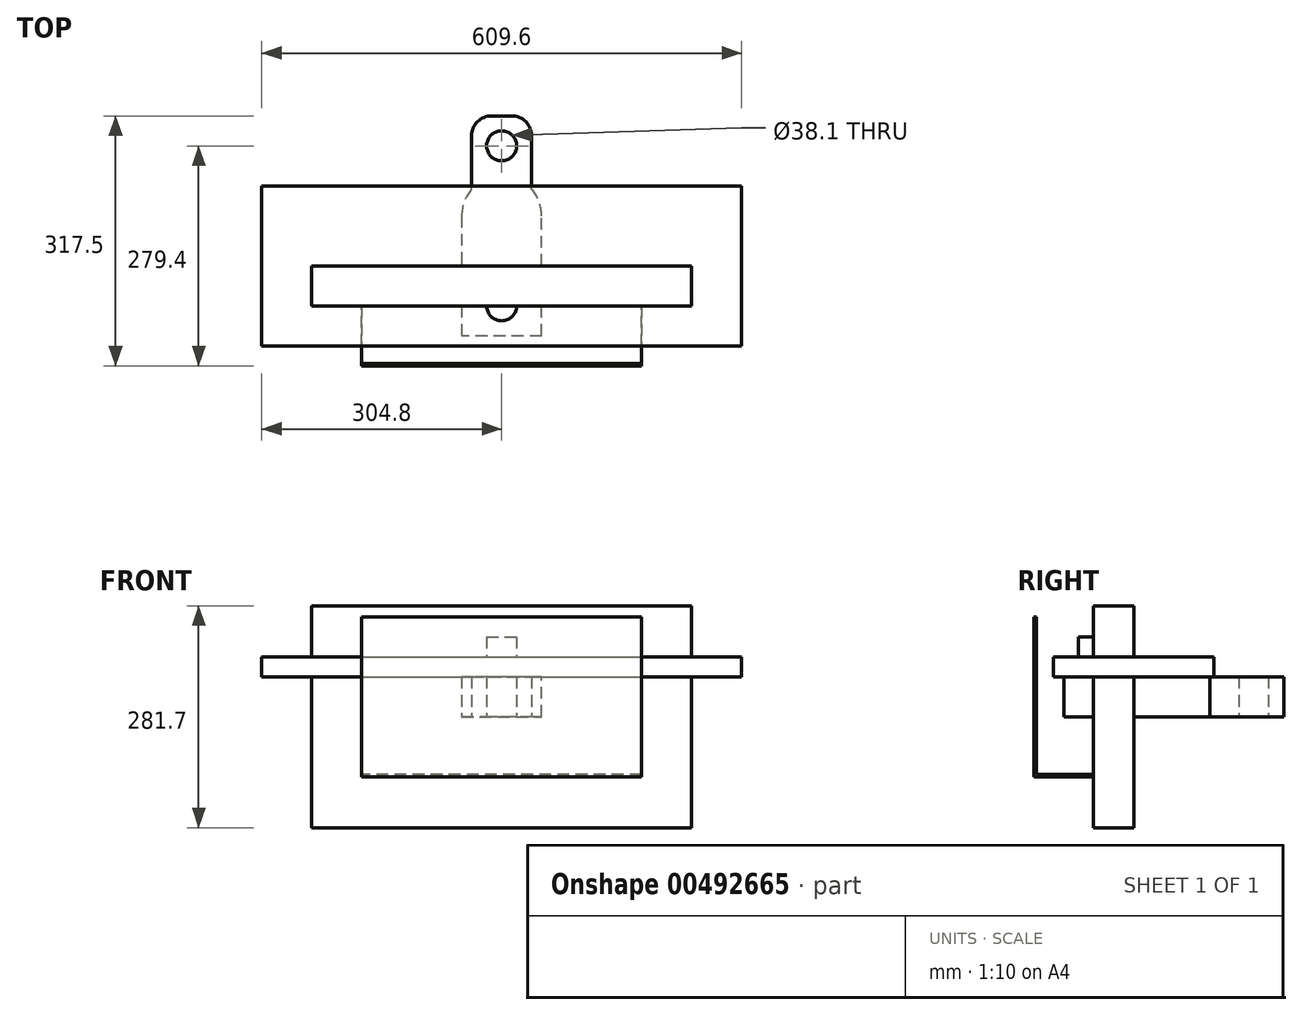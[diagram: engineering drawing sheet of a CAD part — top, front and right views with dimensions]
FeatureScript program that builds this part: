
annotation { "Feature Type Name" : "Feature", "Feature Type Description" : "" }
export const myFeature = defineFeature(function(context is Context, id is Id, definition is map)
    precondition{}
    {
        {
            var Q0;
            Q0=qCreatedBy(makeId("Top.planeOp"),FACE);
            var sketch = newSketch(context, id + "F0", { "sketchPlane" : qUnion([Q0])});
            skCircle(sketch, "E0", {"center": v(0, 0) * mm, "radius": 50.8 * mm});
            skCircle(sketch, "E1", {"center": v(0, 0) * mm, "radius": 25.4 * mm});
            skLineSegment(sketch, "E2.bottom", {"start": v(-50.8, 0) * mm, "end": v(50.8, 0) * mm, "construction": true});
            skLineSegment(sketch, "E2.top", {"start": v(-50.8, -152.4) * mm, "end": v(50.8, -152.4) * mm, "construction": true});
            skLineSegment(sketch, "E2.left", {"start": v(-50.8, 0) * mm, "end": v(-50.8, -152.4) * mm, "construction": true});
            skLineSegment(sketch, "E2.right", {"start": v(50.8, 0) * mm, "end": v(50.8, -152.4) * mm, "construction": true});
            skPoint(sketch, "E2.middle", {"position": v(0, -76.2) * mm});
            skLineSegment(sketch, "E3", {"start": v(-50.8, 0) * mm, "end": v(-50.8, -152.4) * mm});
            skLineSegment(sketch, "E4", {"start": v(50.8, -152.4) * mm, "end": v(50.8, 0) * mm});
            skLineSegment(sketch, "E5", {"start": v(50.8, -152.4) * mm, "end": v(-50.8, -152.4) * mm});
            skSolve(sketch);
        }
        {
            var Q0;
            Q0 = qSketchRegion(id + "F0", true);
            extrude(context, id + "F1", {"entities" : qUnion([Q0]), "depth" : 50.8 * mm, "offsetDistance" : 25 * mm});
        }
        {
            var Q0;
            Q0=makeQuery(id+"F1.opExtrude","CAP_FACE",FACE,{"disambiguationData":[OSD([sQuery(id+"F0.wireOp",EDGE,"E0"),sQuery(id+"F0.wireOp",EDGE,"E1"),sQuery(id+"F0.wireOp",EDGE,"E3"),sQuery(id+"F0.wireOp",EDGE,"E4"),sQuery(id+"F0.wireOp",EDGE,"E5")])],"isStart":false});
            var sketch = newSketch(context, id + "F2", { "sketchPlane" : qUnion([Q0])});
            skLineSegment(sketch, "E6", {"start": v(0, -152.4) * mm, "end": v(0, 0) * mm, "construction": true});
            skCircle(sketch, "E7", {"center": v(0, -114.3) * mm, "radius": 19.05 * mm});
            skSolve(sketch);
        }
        {
            var Q0;
            Q0 = qSketchRegion(id + "F2", true);
            extrude(context, id + "F3", {"entities" : qUnion([Q0]), "operationType" : NewBodyOperationType.ADD, "depth" : 50.8 * mm, "offsetDistance" : 25 * mm});
        }
        {
            var Q0;
            Q0=qCreatedBy(makeId("Top.planeOp"),FACE);
            var sketch = newSketch(context, id + "F4", { "sketchPlane" : qUnion([Q0])});
            skLineSegment(sketch, "E8.bottom", {"start": v(38.1, -127) * mm, "end": v(-38.1, -127) * mm});
            skLineSegment(sketch, "E8.top", {"start": v(38.1, 127) * mm, "end": v(-38.1, 127) * mm});
            skLineSegment(sketch, "E8.left", {"start": v(38.1, -127) * mm, "end": v(38.1, 127) * mm});
            skLineSegment(sketch, "E8.right", {"start": v(-38.1, -127) * mm, "end": v(-38.1, 127) * mm});
            skPoint(sketch, "E8.middle", {"position": v(0, 0) * mm});
            skLineSegment(sketch, "E9", {"start": v(0, 127) * mm, "end": v(0, -127) * mm, "construction": true});
            skCircle(sketch, "E10", {"center": v(0, 88.9) * mm, "radius": 19.05 * mm});
            skSolve(sketch);
        }
        {
            var Q0;
            Q0 = qSketchRegion(id + "F4", true);
            extrude(context, id + "F5", {"entities" : qUnion([Q0]), "depth" : 50.8 * mm, "offsetDistance" : 25 * mm});
        }
        {
            var Q0;
            Q0=makeQuery(id+"F5.opExtrude","CAP_FACE",FACE,{"disambiguationData":[OSD([sQuery(id+"F4.wireOp",EDGE,"E8.bottom"),sQuery(id+"F4.wireOp",EDGE,"E8.top"),sQuery(id+"F4.wireOp",EDGE,"E8.left"),sQuery(id+"F4.wireOp",EDGE,"E8.right"),sQuery(id+"F4.wireOp",EDGE,"E10")])],"isStart":false});
            var sketch = newSketch(context, id + "F6", { "sketchPlane" : qUnion([Q0])});
            skCircle(sketch, "E11", {"center": v(0, -88.9) * mm, "radius": 19.05 * mm});
            skPoint(sketch, "E11.centerSnap0", {"position": v(0, -127) * mm});
            skSolve(sketch);
        }
        {
            var Q0;
            Q0 = qSketchRegion(id + "F6", true);
            extrude(context, id + "F7", {"entities" : qUnion([Q0]), "operationType" : NewBodyOperationType.ADD, "depth" : 50.8 * mm, "offsetDistance" : 25 * mm});
        }
        {
            var Q0;
            Q0=makeQuery(id+"F5.opExtrude","SWEPT_EDGE",EDGE,{"disambiguationData":[OSD([sQuery(id+"F4.wireOp",EDGE,"E8.bottom"),sQuery(id+"F4.wireOp",EDGE,"E8.right")])]});
            var Q1;
            Q1=makeQuery(id+"F5.opExtrude","SWEPT_EDGE",EDGE,{"disambiguationData":[OSD([sQuery(id+"F4.wireOp",EDGE,"E8.bottom"),sQuery(id+"F4.wireOp",EDGE,"E8.left")])]});
            var Q2;
            Q2=makeQuery(id+"F5.opExtrude","SWEPT_EDGE",EDGE,{"disambiguationData":[OSD([sQuery(id+"F4.wireOp",EDGE,"E8.top"),sQuery(id+"F4.wireOp",EDGE,"E8.left")])]});
            var Q3;
            Q3=makeQuery(id+"F5.opExtrude","SWEPT_EDGE",EDGE,{"disambiguationData":[OSD([sQuery(id+"F4.wireOp",EDGE,"E8.top"),sQuery(id+"F4.wireOp",EDGE,"E8.right")])]});
            fillet(context, id + "F8", {"entities" : qUnion([Q0, Q1, Q2, Q3]), "radius" : 25.4 * mm, "tangentPropagation" : true, "allowEdgeOverflow" : false});
        }
        {
            var Q0;
            Q0=qCreatedBy(makeId("Top.planeOp"),FACE);
            var sketch = newSketch(context, id + "F9", { "sketchPlane" : qUnion([Q0])});
            skCircle(sketch, "E12", {"center": v(0, 0) * mm, "radius": 38.1 * mm});
            skCircle(sketch, "E13", {"center": v(0, 0) * mm, "radius": 19.05 * mm});
            skSolve(sketch);
        }
        {
            var Q0;
            Q0 = qSketchRegion(id + "F9", true);
            extrude(context, id + "F10", {"entities" : qUnion([Q0]), "depth" : 50.8 * mm, "offsetDistance" : 25 * mm});
        }
        {
            var Q0;
            Q0=makeQuery(id+"F10.opExtrude","CAP_FACE",FACE,{"disambiguationData":[OSD([sQuery(id+"F9.wireOp",EDGE,"E12"),sQuery(id+"F9.wireOp",EDGE,"E13")])],"isStart":false});
            var sketch = newSketch(context, id + "F11", { "sketchPlane" : qUnion([Q0])});
            skLineSegment(sketch, "E14.bottom", {"start": v(-304.8, 38.1) * mm, "end": v(304.8, 38.1) * mm});
            skLineSegment(sketch, "E14.top", {"start": v(-304.8, -165.1) * mm, "end": v(304.8, -165.1) * mm});
            skLineSegment(sketch, "E14.left", {"start": v(-304.8, 38.1) * mm, "end": v(-304.8, -165.1) * mm});
            skLineSegment(sketch, "E14.right", {"start": v(304.8, 38.1) * mm, "end": v(304.8, -165.1) * mm});
            skPoint(sketch, "E14.middle", {"position": v(0, -63.5) * mm});
            skSolve(sketch);
        }
        {
            var Q0;
            Q0 = qSketchRegion(id + "F11", true);
            extrude(context, id + "F12", {"entities" : qUnion([Q0]), "operationType" : NewBodyOperationType.ADD, "depth" : 25.4 * mm, "offsetDistance" : 25 * mm});
        }
        {
            var Q0;
            Q0=qCreatedBy(makeId("Top.planeOp"),FACE);
            var sketch = newSketch(context, id + "F13", { "sketchPlane" : qUnion([Q0])});
            skCircle(sketch, "E15", {"center": v(0, 0) * mm, "radius": 19.05 * mm});
            skCircle(sketch, "E16", {"center": v(0, 0) * mm, "radius": 38.1 * mm});
            skLineSegment(sketch, "E17", {"start": v(-38.1, 0) * mm, "end": v(-38.1, -63.5) * mm});
            skLineSegment(sketch, "E18", {"start": v(-38.1, -63.5) * mm, "end": v(38.1, -63.5) * mm});
            skLineSegment(sketch, "E19", {"start": v(38.1, -63.5) * mm, "end": v(38.1, 0) * mm});
            skSolve(sketch);
        }
        {
            var Q0;
            Q0 = qSketchRegion(id + "F13", true);
            extrude(context, id + "F14", {"entities" : qUnion([Q0]), "depth" : 50.8 * mm, "offsetDistance" : 25 * mm});
        }
        {
            var Q0;
            Q0=makeQuery(id+"F14.opExtrude","SWEPT_FACE",FACE,{"disambiguationData":[OSD([sQuery(id+"F13.wireOp",EDGE,"E18")])]});
            var sketch = newSketch(context, id + "F15", { "sketchPlane" : qUnion([Q0])});
            skLineSegment(sketch, "E20.bottom", {"start": v(241.3, -140.85) * mm, "end": v(-241.3, -140.85) * mm});
            skLineSegment(sketch, "E20.top", {"start": v(241.3, 140.85) * mm, "end": v(-241.3, 140.85) * mm});
            skLineSegment(sketch, "E20.left", {"start": v(241.3, -140.85) * mm, "end": v(241.3, 140.85) * mm});
            skLineSegment(sketch, "E20.right", {"start": v(-241.3, -140.85) * mm, "end": v(-241.3, 140.85) * mm});
            skPoint(sketch, "E20.middle", {"position": v(0, 0) * mm});
            skSolve(sketch);
        }
        {
            var Q0;
            Q0 = qSketchRegion(id + "F15", true);
            extrude(context, id + "F16", {"entities" : qUnion([Q0]), "operationType" : NewBodyOperationType.ADD, "depth" : 50.8 * mm, "offsetDistance" : 25 * mm});
        }
        {
            var Q0;
            Q0=qCreatedBy(makeId("Top.planeOp"),FACE);
            var sketch = newSketch(context, id + "F17", { "sketchPlane" : qUnion([Q0])});
            skCircle(sketch, "E21", {"center": v(0, 0) * mm, "radius": 50.8 * mm});
            skCircle(sketch, "E22", {"center": v(0, 0) * mm, "radius": 25.4 * mm});
            skLineSegment(sketch, "E23", {"start": v(-50.8, 0) * mm, "end": v(-50.8, -76.2) * mm});
            skLineSegment(sketch, "E24", {"start": v(-50.8, -76.2) * mm, "end": v(50.8, -76.2) * mm});
            skLineSegment(sketch, "E25", {"start": v(50.8, -76.2) * mm, "end": v(50.8, 0) * mm});
            skSolve(sketch);
        }
        {
            var Q0;
            Q0 = qSketchRegion(id + "F17", true);
            extrude(context, id + "F18", {"entities" : qUnion([Q0]), "depth" : 50.8 * mm, "offsetDistance" : 25 * mm});
        }
        {
            var Q0;
            Q0=qCreatedBy(makeId("Right.planeOp"),FACE);
            var sketch = newSketch(context, id + "F19", { "sketchPlane" : qUnion([Q0])});
            skLineSegment(sketch, "E26.0", {"start": v(-76.2, 50.8) * mm, "end": v(-76.2, 0) * mm});
            skLineSegment(sketch, "E27", {"start": v(-76.2, 50.8) * mm, "end": v(-76.2, 0) * mm, "construction": true});
            skLineSegment(sketch, "E28.bottom", {"start": v(-76.2, -76.2) * mm, "end": v(-190.5, -76.2) * mm});
            skLineSegment(sketch, "E28.top", {"start": v(-76.2, 127) * mm, "end": v(-190.5, 127) * mm});
            skLineSegment(sketch, "E28.left", {"start": v(-76.2, -76.2) * mm, "end": v(-76.2, 127) * mm});
            skLineSegment(sketch, "E28.right", {"start": v(-190.5, -76.2) * mm, "end": v(-190.5, 127) * mm});
            skPoint(sketch, "E28.middle", {"position": v(-133.35, 25.4) * mm});
            skLineSegment(sketch, "E29.bottom", {"start": v(-187.33, 127) * mm, "end": v(-79.38, 127) * mm});
            skLineSegment(sketch, "E29.top", {"start": v(-187.32, -73.03) * mm, "end": v(-79.37, -73.02) * mm});
            skLineSegment(sketch, "E29.left", {"start": v(-187.33, 127) * mm, "end": v(-187.32, -73.03) * mm});
            skLineSegment(sketch, "E29.right", {"start": v(-79.38, 127) * mm, "end": v(-79.37, -73.02) * mm});
            skSolve(sketch);
        }
        {
            var Q0;
            {var subQ1=sQuery(id+"F19.wireOp",EDGE,"E28.bottom");Q0=makeQuery(id+"F19.imprint","IMPRINT",FACE,{"disambiguationData":[TD([[makeQuery(id+"F19.imprint","IMPRINT",EDGE,{"derivedFrom":subQ1}),-1.0]])]});}
            extrude(context, id + "F20", {"entities" : qUnion([Q0]), "operationType" : NewBodyOperationType.ADD, "depth" : 177.8 * mm, "offsetDistance" : 25 * mm, "hasSecondDirection" : true, "secondDirectionOppositeDirection" : true, "secondDirectionDepth" : 177.8 * mm});
        }
    });
